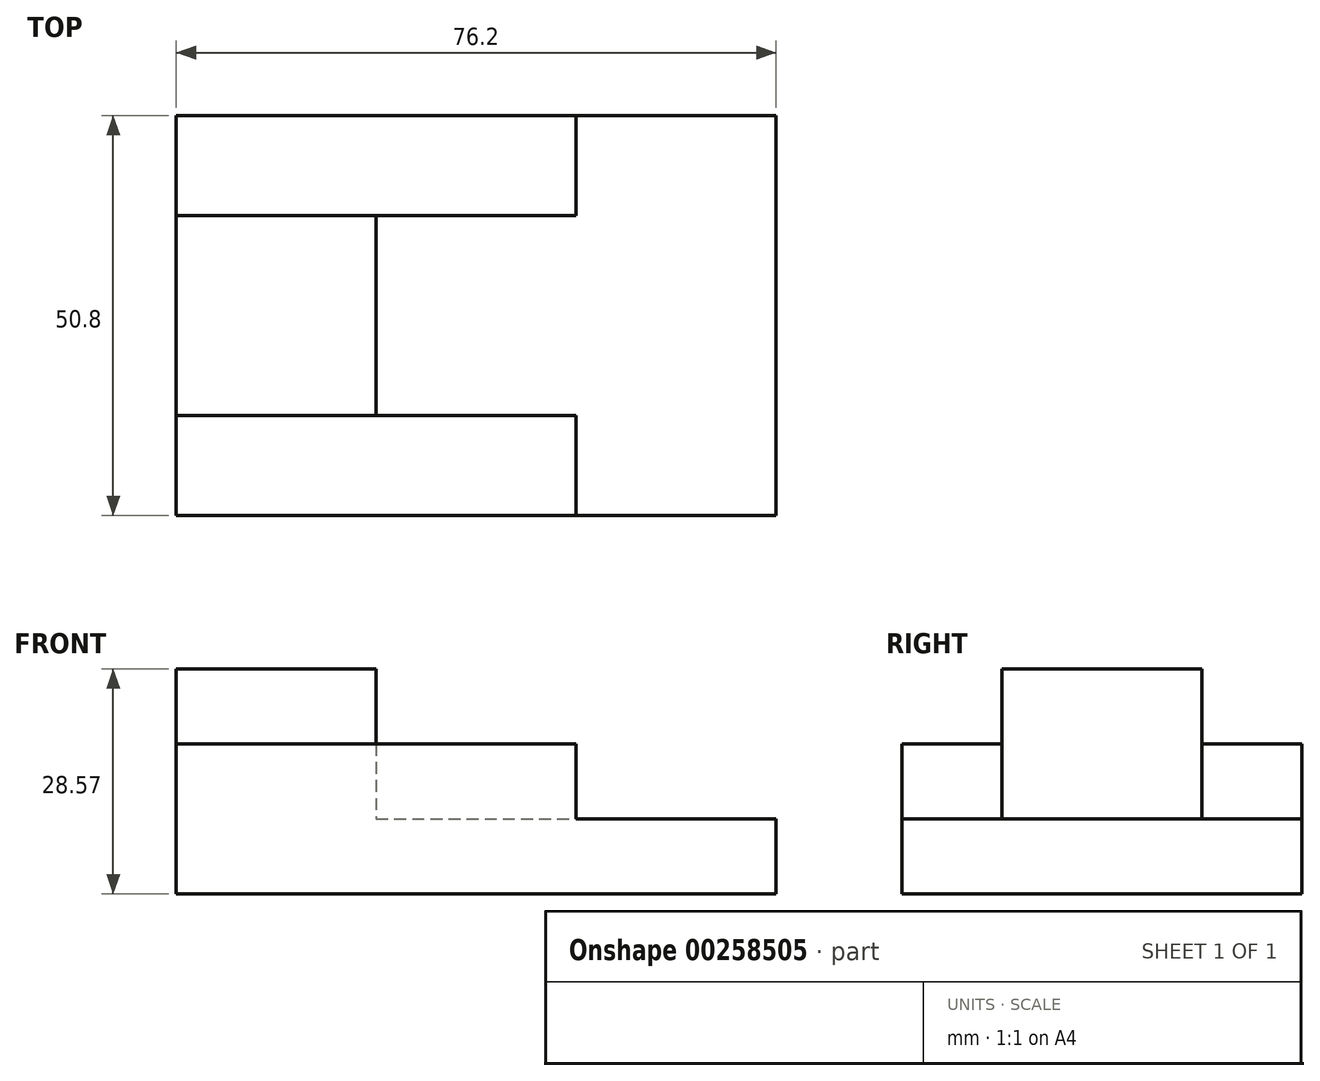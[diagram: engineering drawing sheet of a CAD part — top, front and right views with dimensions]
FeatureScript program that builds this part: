
annotation { "Feature Type Name" : "Feature", "Feature Type Description" : "" }
export const myFeature = defineFeature(function(context is Context, id is Id, definition is map)
    precondition{}
    {
        {
            var Q0;
            Q0=qCreatedBy(makeId("Top.planeOp"),FACE);
            var sketch = newSketch(context, id + "F0", { "sketchPlane" : qUnion([Q0])});
            skLineSegment(sketch, "E0.bottom", {"start": v(-38.1, -25.4) * mm, "end": v(38.1, -25.4) * mm});
            skLineSegment(sketch, "E0.top", {"start": v(-38.1, 25.4) * mm, "end": v(38.1, 25.4) * mm});
            skLineSegment(sketch, "E0.left", {"start": v(-38.1, -25.4) * mm, "end": v(-38.1, 25.4) * mm});
            skLineSegment(sketch, "E0.right", {"start": v(38.1, -25.4) * mm, "end": v(38.1, 25.4) * mm});
            skPoint(sketch, "E0.middle", {"position": v(0, 0) * mm});
            skSolve(sketch);
        }
        {
            var Q0;
            Q0=makeQuery(id+"F0.imprint","IMPRINT",FACE,{"disambiguationData":[TD([[makeQuery(id+"F0.imprint","IMPRINT",EDGE,{"derivedFrom":sQuery(id+"F0.wireOp",EDGE,"E0.bottom")}),1.0]])]});
            extrude(context, id + "F1", {"entities" : qUnion([Q0]), "depth" : 9.52 * mm});
        }
        {
            var Q0;
            Q0=makeQuery(id+"F1.opExtrude","CAP_FACE",FACE,{"disambiguationData":[OSD([sQuery(id+"F0.wireOp",EDGE,"E0.bottom"),sQuery(id+"F0.wireOp",EDGE,"E0.top"),sQuery(id+"F0.wireOp",EDGE,"E0.left"),sQuery(id+"F0.wireOp",EDGE,"E0.right")])],"isStart":false});
            var sketch = newSketch(context, id + "F2", { "sketchPlane" : qUnion([Q0])});
            skLineSegment(sketch, "E1.bottom", {"start": v(-38.1, 25.4) * mm, "end": v(12.7, 25.4) * mm});
            skLineSegment(sketch, "E1.top", {"start": v(-38.1, 12.7) * mm, "end": v(12.7, 12.7) * mm});
            skLineSegment(sketch, "E1.left", {"start": v(-38.1, 25.4) * mm, "end": v(-38.1, 12.7) * mm});
            skLineSegment(sketch, "E1.right", {"start": v(12.7, 25.4) * mm, "end": v(12.7, 12.7) * mm});
            skLineSegment(sketch, "E2.bottom", {"start": v(-38.1, -25.4) * mm, "end": v(12.7, -25.4) * mm});
            skLineSegment(sketch, "E2.top", {"start": v(-38.1, -12.7) * mm, "end": v(12.7, -12.7) * mm});
            skLineSegment(sketch, "E2.left", {"start": v(-38.1, -25.4) * mm, "end": v(-38.1, -12.7) * mm});
            skLineSegment(sketch, "E2.right", {"start": v(12.7, -25.4) * mm, "end": v(12.7, -12.7) * mm});
            skLineSegment(sketch, "E3.bottom", {"start": v(-38.1, 25.4) * mm, "end": v(-12.7, 25.4) * mm});
            skLineSegment(sketch, "E3.top", {"start": v(-38.1, -25.4) * mm, "end": v(-12.7, -25.4) * mm});
            skLineSegment(sketch, "E3.left", {"start": v(-38.1, 25.4) * mm, "end": v(-38.1, -25.4) * mm});
            skLineSegment(sketch, "E3.right", {"start": v(-12.7, 25.4) * mm, "end": v(-12.7, -25.4) * mm});
            skSolve(sketch);
        }
        {
            var Q0;
            {var subQ5=sQuery(id+"F2.wireOp",EDGE,"E3.bottom");Q0=makeQuery(id+"F2.imprint","IMPRINT",FACE,{"disambiguationData":[TD([[makeQuery(id+"F2.imprint","IMPRINT",EDGE,{"derivedFrom":subQ5}),-1.0]])]});}
            var Q1;
            {var subQ0=sQuery(id+"F2.wireOp",EDGE,"E3.left");var subQ1=sQuery(id+"F2.wireOp",EDGE,"E1.top");var subQ2=makeQuery(id+"F2.imprint","INTERSECT",VERTEX,{"derivedFrom":[subQ1,subQ0]});Q1=makeQuery(id+"F2.imprint","IMPRINT",FACE,{"disambiguationData":[TD([[makeQuery(id+"F2.imprint","IMPRINT",EDGE,{"disambiguationData":[TD([[subQ2,-1.0]])],"derivedFrom":subQ1}),-1.0]])]});}
            var Q2;
            {var subQ5=sQuery(id+"F2.wireOp",EDGE,"E3.top");Q2=makeQuery(id+"F2.imprint","IMPRINT",FACE,{"disambiguationData":[TD([[makeQuery(id+"F2.imprint","IMPRINT",EDGE,{"derivedFrom":subQ5}),1.0]])]});}
            extrude(context, id + "F3", {"entities" : qUnion([Q0, Q1, Q2]), "operationType" : NewBodyOperationType.ADD, "depth" : 19.05 * mm});
        }
        {
            var Q0;
            Q0 = qSketchRegion(id + "F2", true);
            extrude(context, id + "F4", {"entities" : qUnion([Q0]), "operationType" : NewBodyOperationType.ADD, "depth" : 9.52 * mm});
        }
    });
